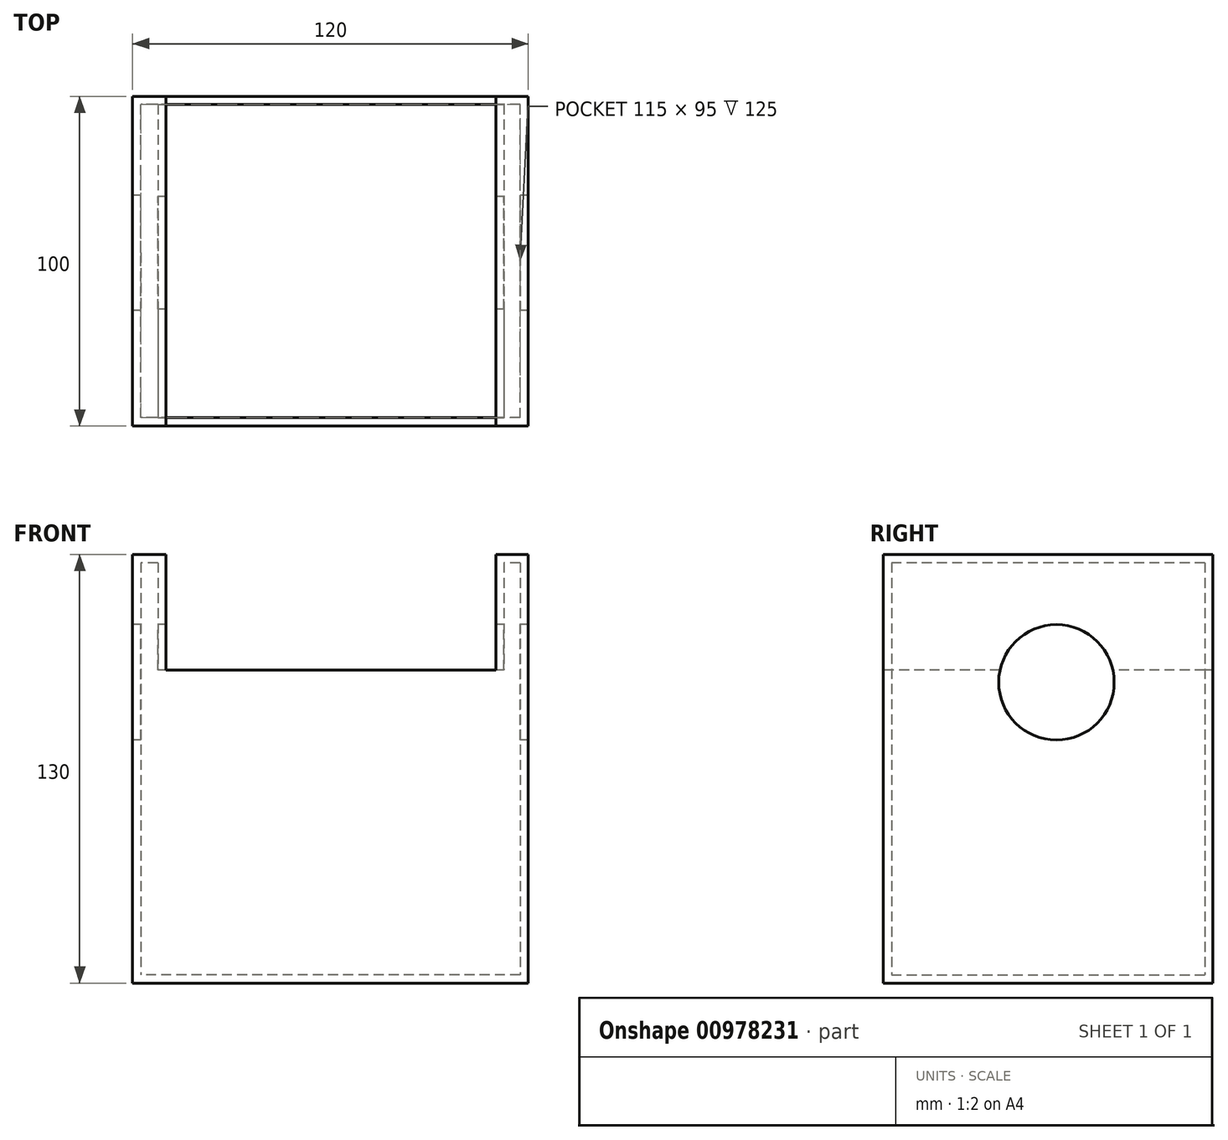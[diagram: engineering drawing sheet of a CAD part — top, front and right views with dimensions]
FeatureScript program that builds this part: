
annotation { "Feature Type Name" : "Feature", "Feature Type Description" : "" }
export const myFeature = defineFeature(function(context is Context, id is Id, definition is map)
    precondition{}
    {
        {
            var Q0;
            Q0=qCreatedBy(makeId("Front.planeOp"),FACE);
            var sketch = newSketch(context, id + "F0", { "sketchPlane" : qUnion([Q0])});
            skLineSegment(sketch, "E0.bottom", {"start": v(59.3, 67.24) * mm, "end": v(-60.7, 67.24) * mm});
            skLineSegment(sketch, "E0.top", {"start": v(59.3, -62.76) * mm, "end": v(-60.7, -62.76) * mm});
            skLineSegment(sketch, "E0.left", {"start": v(59.3, 67.24) * mm, "end": v(59.3, -62.76) * mm});
            skLineSegment(sketch, "E0.right", {"start": v(-60.7, 67.24) * mm, "end": v(-60.7, -62.76) * mm});
            skSolve(sketch);
        }
        {
            var Q0;
            Q0=makeQuery(id+"F0.imprint","IMPRINT",FACE,{"disambiguationData":[TD([[makeQuery(id+"F0.imprint","IMPRINT",EDGE,{"derivedFrom":sQuery(id+"F0.wireOp",EDGE,"E0.bottom")}),1.0]])]});
            extrude(context, id + "F1", {"entities" : qUnion([Q0]), "depth" : 100 * mm, "offsetDistance" : 25 * mm});
        }
        {
            var Q0;
            Q0=makeQuery(id+"F1.opExtrude","CAP_FACE",FACE,{"disambiguationData":[OSD([sQuery(id+"F0.wireOp",EDGE,"E0.bottom"),sQuery(id+"F0.wireOp",EDGE,"E0.top"),sQuery(id+"F0.wireOp",EDGE,"E0.left"),sQuery(id+"F0.wireOp",EDGE,"E0.right")])],"isStart":false});
            var sketch = newSketch(context, id + "F2", { "sketchPlane" : qUnion([Q0])});
            skLineSegment(sketch, "E1.bottom", {"start": v(-50.56, 67.24) * mm, "end": v(49.44, 67.24) * mm});
            skLineSegment(sketch, "E1.top", {"start": v(-50.56, 32.24) * mm, "end": v(49.44, 32.24) * mm});
            skLineSegment(sketch, "E1.left", {"start": v(-50.56, 67.24) * mm, "end": v(-50.56, 32.24) * mm});
            skLineSegment(sketch, "E1.right", {"start": v(49.44, 67.24) * mm, "end": v(49.44, 32.24) * mm});
            skSolve(sketch);
        }
        {
            var Q0;
            Q0=makeQuery(id+"F2.imprint","IMPRINT",FACE,{"disambiguationData":[TD([[makeQuery(id+"F2.imprint","IMPRINT",EDGE,{"derivedFrom":sQuery(id+"F2.wireOp",EDGE,"E1.bottom")}),1.0]])]});
            extrude(context, id + "F3", {"entities" : qUnion([Q0]), "operationType" : NewBodyOperationType.REMOVE, "oppositeDirection" : true, "depth" : 125 * mm, "offsetDistance" : 25 * mm});
        }
        {
            var Q0;
            Q0=makeQuery(id+"F3.boolean.opBoolean","COPY",FACE,{"derivedFrom":makeQuery(id+"F3.opExtrude","SWEPT_FACE",FACE,{"disambiguationData":[OSD([sQuery(id+"F2.wireOp",EDGE,"E1.top")])]})});
            shell(context, id + "F4", {"entities" : qUnion([Q0]), "thickness" : 2.5 * mm});
        }
        {
            var Q0;
            Q0=makeQuery(id+"F1.opExtrude","SWEPT_FACE",FACE,{"disambiguationData":[OSD([sQuery(id+"F0.wireOp",EDGE,"E0.right")])]});
            var sketch = newSketch(context, id + "F5", { "sketchPlane" : qUnion([Q0])});
            skCircle(sketch, "E2", {"center": v(47.48, 28.47) * mm, "radius": 17.5 * mm});
            skSolve(sketch);
        }
        {
            var Q0;
            Q0=makeQuery(id+"F5.imprint","IMPRINT",FACE,{"disambiguationData":[TD([[makeQuery(id+"F5.imprint","IMPRINT",EDGE,{"derivedFrom":sQuery(id+"F5.wireOp",EDGE,"E2")}),1.0]])]});
            extrude(context, id + "F6", {"entities" : qUnion([Q0]), "operationType" : NewBodyOperationType.REMOVE, "oppositeDirection" : true, "depth" : 5005 * mm, "offsetDistance" : 25 * mm});
        }
    });
